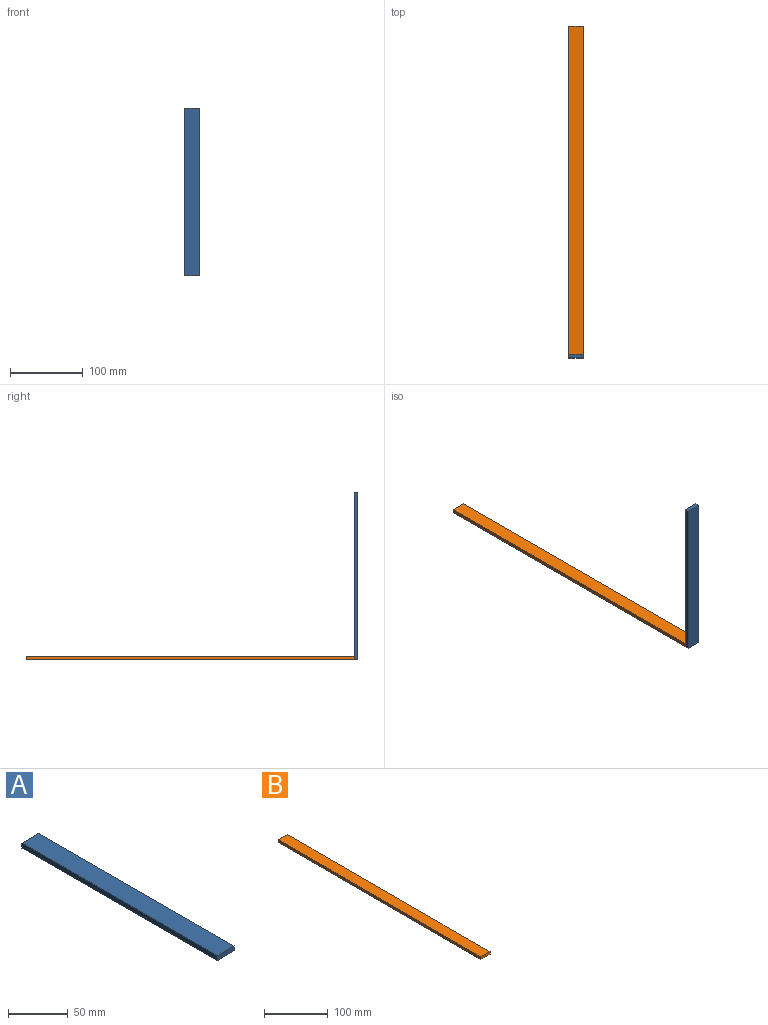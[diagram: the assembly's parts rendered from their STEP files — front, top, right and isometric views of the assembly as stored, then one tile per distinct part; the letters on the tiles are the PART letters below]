
ASSEMBLY  parts=2 mates=1
PART A: 6 faces, bbox 20x230x5 mm
  f0: plane 230x20mm, normal (0,0,1), area 4600mm2, adj f1,f3,f4,f5
  f1: plane 230x5mm, normal (-1,0,0), area 1150mm2, adj f0,f2,f4,f5
  f2: plane 230x20mm, normal (0,0,-1), area 4600mm2, adj f1,f3,f4,f5
  f3: plane 230x5mm, normal (1,0,0), area 1150mm2, adj f0,f2,f4,f5
  f4: plane 20x5mm, normal (0,-1,0), area 100mm2, adj f0,f1,f2,f3
  f5: plane 20x5mm, normal (0,1,0), area 100mm2, adj f0,f1,f2,f3
PART B: 6 faces, bbox 20x450x5 mm
  f0: plane 450x20mm, normal (0,0,1), area 9000mm2, adj f1,f3,f4,f5
  f1: plane 450x5mm, normal (-1,0,0), area 2250mm2, adj f0,f2,f4,f5
  f2: plane 450x20mm, normal (0,0,-1), area 9000mm2, adj f1,f3,f4,f5
  f3: plane 450x5mm, normal (1,0,0), area 2250mm2, adj f0,f2,f4,f5
  f4: plane 20x5mm, normal (0,-1,0), area 100mm2, adj f0,f1,f2,f3
  f5: plane 20x5mm, normal (0,1,0), area 100mm2, adj f0,f1,f2,f3
PLACE A rot(axis=(-1,0,0),90deg) t=(-145.94,-352.31,-63.33)mm
PLACE B t=(-145.94,100.19,-60.83)mm
MATE fastened A.f0 <-> B.f4  axis (0,1,0) through (-145.94,-349.81,-63.33)mm
